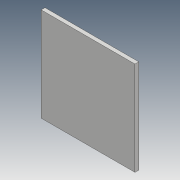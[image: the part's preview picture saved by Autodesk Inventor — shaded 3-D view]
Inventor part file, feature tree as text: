
AUTODESK INVENTOR PART (.ipt)
format: ipt  version: 2017 (Build 210142000, 142)  size: 80,896 bytes
history: native  units: mm
features: extrude x1, sketch x1
ambient origin geometry x8: Origin, YZ Plane, XZ Plane, XY Plane, X Axis, Y Axis, Z Axis, Center Point
bodies: Solid1 (feature_tree)
feature tree (2):
  extrude  "Extrusion1"  Depth=49.0mm
  sketch  "Sketch1"  dims[d0=49.0mm d1=49.0mm d2=2.0mm d3=0.0mm]
